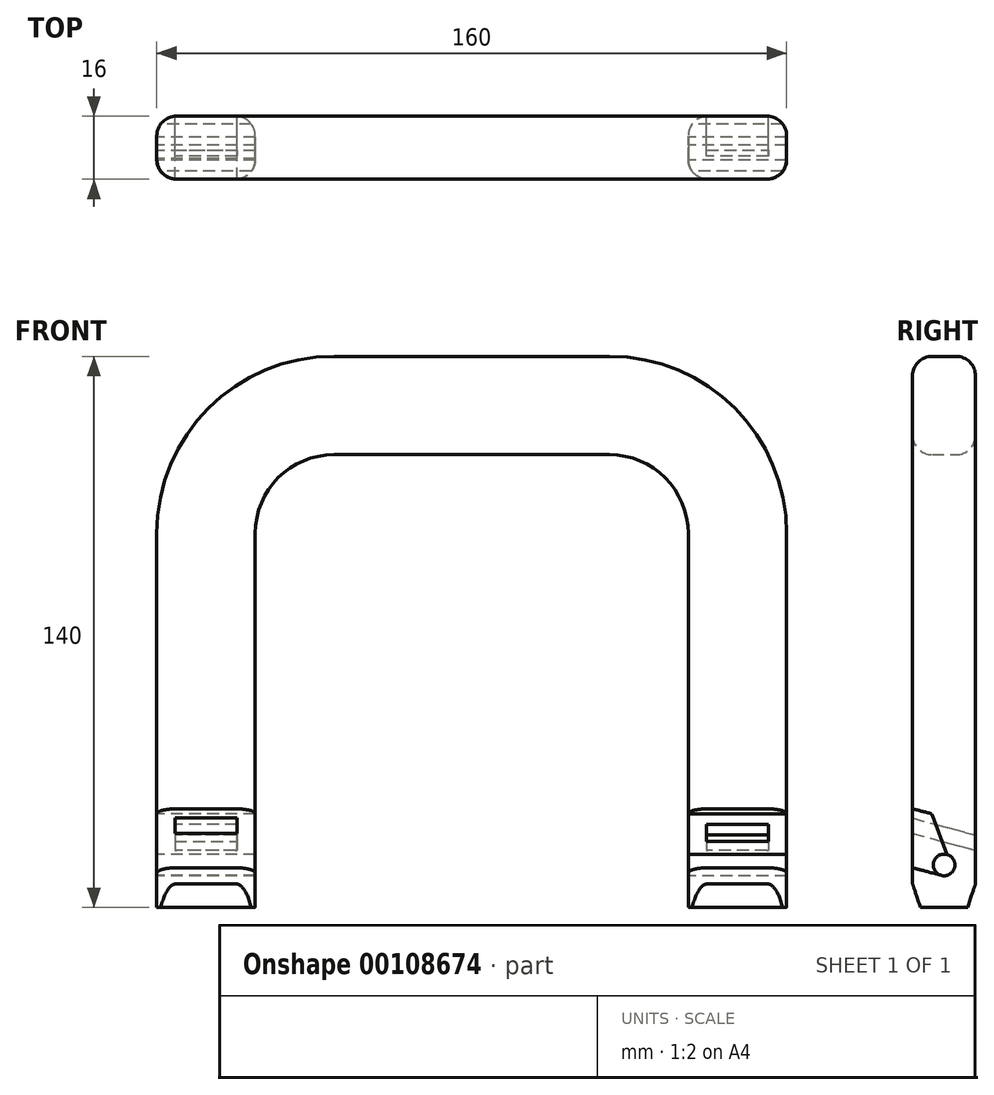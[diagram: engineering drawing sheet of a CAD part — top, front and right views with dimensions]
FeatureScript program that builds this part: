
annotation { "Feature Type Name" : "Feature", "Feature Type Description" : "" }
export const myFeature = defineFeature(function(context is Context, id is Id, definition is map)
    precondition{}
    {
        {
            var Q0;
            Q0=qCreatedBy(makeId("Front.planeOp"),FACE);
            var sketch = newSketch(context, id + "F0", { "sketchPlane" : qUnion([Q0])});
            skLineSegment(sketch, "E0.bottom", {"start": v(-80, 0) * mm, "end": v(80, 0) * mm});
            skLineSegment(sketch, "E0.top", {"start": v(-35, 140) * mm, "end": v(35, 140) * mm});
            skLineSegment(sketch, "E0.left", {"start": v(-80, 0) * mm, "end": v(-80, 95) * mm});
            skLineSegment(sketch, "E0.right", {"start": v(80, 0) * mm, "end": v(80, 95) * mm});
            skLineSegment(sketch, "E1.bottom", {"start": v(-55, 0) * mm, "end": v(55, 0) * mm});
            skLineSegment(sketch, "E1.top", {"start": v(-35, 115) * mm, "end": v(35, 115) * mm});
            skLineSegment(sketch, "E1.left", {"start": v(-55, 0) * mm, "end": v(-55, 95) * mm});
            skLineSegment(sketch, "E1.right", {"start": v(55, 0) * mm, "end": v(55, 95) * mm});
            skPoint(sketch, "E2.visualSharp", {"position": v(-80, 140) * mm});
            skArc(sketch, "E2.filletArc", {"start": v(-35, 140) * mm, "mid": v(-66.82, 126.82) * mm, "end": v(-80, 95) * mm});
            skPoint(sketch, "E3.visualSharp", {"position": v(80, 140) * mm});
            skArc(sketch, "E3.filletArc", {"start": v(80, 95) * mm, "mid": v(66.82, 126.82) * mm, "end": v(35, 140) * mm});
            skPoint(sketch, "E4.visualSharp", {"position": v(-55, 115) * mm});
            skArc(sketch, "E4.filletArc", {"start": v(-35, 115) * mm, "mid": v(-49.14, 109.14) * mm, "end": v(-55, 95) * mm});
            skPoint(sketch, "E5.visualSharp", {"position": v(55, 115) * mm});
            skArc(sketch, "E5.filletArc", {"start": v(55, 95) * mm, "mid": v(49.14, 109.14) * mm, "end": v(35, 115) * mm});
            skSolve(sketch);
        }
        {
            var Q0;
            Q0=makeQuery(id+"F0.imprint","IMPRINT",FACE,{"disambiguationData":[TD([[makeQuery(id+"F0.imprint","IMPRINT",EDGE,{"derivedFrom":sQuery(id+"F0.wireOp",EDGE,"E0.top")}),-1.0]])]});
            extrude(context, id + "F1", {"entities" : qUnion([Q0]), "depth" : 16 * mm});
        }
        {
            var Q0;
            Q0=makeQuery(id+"F1.opExtrude","SWEPT_FACE",FACE,{"disambiguationData":[OSD([sQuery(id+"F0.wireOp",EDGE,"E0.left")])]});
            var sketch = newSketch(context, id + "F2", { "sketchPlane" : qUnion([Q0])});
            skCircle(sketch, "E6", {"center": v(8, 10.75) * mm, "radius": 2.75 * mm});
            skLineSegment(sketch, "E7", {"start": v(8, 0) * mm, "end": v(8, 10.75) * mm, "construction": true});
            skLineSegment(sketch, "E8", {"start": v(8.71, 8.1) * mm, "end": v(16, 10.05) * mm});
            skLineSegment(sketch, "E9", {"start": v(16, 6) * mm, "end": v(14, 0) * mm});
            skLineSegment(sketch, "E10", {"start": v(2, 0) * mm, "end": v(0, 6) * mm});
            skLineSegment(sketch, "E11", {"start": v(11.17, 23.75) * mm, "end": v(16, 25.05) * mm});
            skLineSegment(sketch, "E12", {"start": v(8.71, 8.1) * mm, "end": v(8, 10.75) * mm, "construction": true});
            skLineSegment(sketch, "E13", {"start": v(8, 10.75) * mm, "end": v(7.29, 13.4) * mm, "construction": true});
            skLineSegment(sketch, "E14", {"start": v(7.29, 13.4) * mm, "end": v(11.17, 23.75) * mm});
            skLineSegment(sketch, "E15", {"start": v(11.17, 23.75) * mm, "end": v(0, 20.76) * mm});
            skSolve(sketch);
        }
        {
            var Q0;
            Q0 = qSketchRegion(id + "F2", true);
            var Q1;
            {var subQ0=sQuery(id+"F2.wireOp",EDGE,"E10");Q1=makeQuery(id+"F2.imprint","IMPRINT",FACE,{"disambiguationData":[TD([[makeQuery(id+"F2.imprint","IMPRINT",EDGE,{"derivedFrom":subQ0}),1.0]])]});}
            var Q2;
            {var subQ0=sQuery(id+"F2.wireOp",EDGE,"E9");Q2=makeQuery(id+"F2.imprint","IMPRINT",FACE,{"disambiguationData":[TD([[makeQuery(id+"F2.imprint","IMPRINT",EDGE,{"derivedFrom":subQ0}),1.0]])]});}
            var Q3;
            {var subQ0=sQuery(id+"F2.wireOp",EDGE,"E8");Q3=makeQuery(id+"F2.imprint","IMPRINT",FACE,{"disambiguationData":[TD([[makeQuery(id+"F2.imprint","IMPRINT",EDGE,{"derivedFrom":subQ0}),1.0]])]});}
            extrude(context, id + "F3", {"entities" : qUnion([Q0, Q1, Q2, Q3]), "operationType" : NewBodyOperationType.REMOVE, "endBound" : BoundingType.THROUGH_ALL, "oppositeDirection" : true, "depth" : 25 * mm});
        }
        {
            var Q0;
            {var subQ2=sQuery(id+"F2.wireOp",EDGE,"E8");Q0=makeQuery(id+"F2.imprint","IMPRINT",FACE,{"disambiguationData":[TD([[makeQuery(id+"F2.imprint","IMPRINT",EDGE,{"derivedFrom":subQ2}),1.0]])]});}
            extrude(context, id + "F4", {"entities" : qUnion([Q0]), "oppositeDirection" : true, "depth" : 25 * mm});
        }
        {
            var Q0;
            Q0=makeQuery(id+"F4.opExtrude","SWEPT_FACE",FACE,{"disambiguationData":[OSD([sQuery(id+"F0.wireOp",EDGE,"E0.left")])]});
            var sketch = newSketch(context, id + "F5", { "sketchPlane" : qUnion([Q0])});
            skLineSegment(sketch, "E16.bottom", {"start": v(-59.62, 22.65) * mm, "end": v(-75.38, 22.65) * mm});
            skLineSegment(sketch, "E16.top", {"start": v(-59.62, 18.76) * mm, "end": v(-75.38, 18.76) * mm});
            skLineSegment(sketch, "E16.left", {"start": v(-59.62, 22.65) * mm, "end": v(-59.62, 18.76) * mm});
            skLineSegment(sketch, "E16.right", {"start": v(-75.38, 22.65) * mm, "end": v(-75.38, 18.76) * mm});
            skPoint(sketch, "E16.middle", {"position": v(-67.5, 20.7) * mm});
            skLineSegment(sketch, "E17", {"start": v(-67.5, 10.05) * mm, "end": v(-67.5, 20.7) * mm, "construction": true});
            skSolve(sketch);
        }
        {
            var Q0;
            Q0=makeQuery(id+"F5.imprint","IMPRINT",FACE,{"disambiguationData":[TD([[makeQuery(id+"F5.imprint","IMPRINT",EDGE,{"derivedFrom":sQuery(id+"F5.wireOp",EDGE,"E16.bottom")}),1.0]])]});
            var Q1;
            Q1=sQuery(id+"F2.wireOp",EDGE,"E11");
            var Q2;
            Q2=sQuery(id+"F2.wireOp",EDGE,"E15");
            sweep(context, id + "F6", {"profiles" : qUnion([Q0]), "path" : qUnion([Q1, Q2])});
        }
        {
            var Q0;
            Q0=makeQuery(id+"F6.opSweep","SWEPT_BODY",BODY,{"disambiguationData":[OSD([sQuery(id+"F2.wireOp",EDGE,"E15"),sQuery(id+"F5.wireOp",EDGE,"E16.bottom"),sQuery(id+"F5.wireOp",EDGE,"E16.top"),sQuery(id+"F5.wireOp",EDGE,"E16.left"),sQuery(id+"F5.wireOp",EDGE,"E16.right")])]});
            var Q1;
            Q1=makeQuery(id+"F1.opExtrude","CAP_EDGE",EDGE,{"disambiguationData":[OSD([sQuery(id+"F0.wireOp",EDGE,"E0.top")])],"isStart":false});
            transform(context, id + "F7", {"entities" : qUnion([Q0]), "transformType" : TransformType.COPY});
        }
        {
            var Q0;
            Q0=makeQuery(id+"F7.opPattern","COPY",BODY,{"derivedFrom":makeQuery(id+"F6.opSweep","SWEPT_BODY",BODY,{"disambiguationData":[OSD([sQuery(id+"F2.wireOp",EDGE,"E15"),sQuery(id+"F5.wireOp",EDGE,"E16.bottom"),sQuery(id+"F5.wireOp",EDGE,"E16.top"),sQuery(id+"F5.wireOp",EDGE,"E16.left"),sQuery(id+"F5.wireOp",EDGE,"E16.right")])]}),"instanceName":"1"});
            transform(context, id + "F8", {"entities" : qUnion([Q0]), "transformType" : TransformType.COPY});
        }
        {
            var Q0;
            Q0=makeQuery(id+"F8.opPattern","COPY",BODY,{"derivedFrom":makeQuery(id+"F7.opPattern","COPY",BODY,{"derivedFrom":makeQuery(id+"F6.opSweep","SWEPT_BODY",BODY,{"disambiguationData":[OSD([sQuery(id+"F2.wireOp",EDGE,"E15"),sQuery(id+"F5.wireOp",EDGE,"E16.bottom"),sQuery(id+"F5.wireOp",EDGE,"E16.top"),sQuery(id+"F5.wireOp",EDGE,"E16.left"),sQuery(id+"F5.wireOp",EDGE,"E16.right")])]}),"instanceName":"1"}),"instanceName":"1"});
            var Q1;
            Q1=makeQuery(id+"F1.opExtrude","CAP_EDGE",EDGE,{"disambiguationData":[OSD([sQuery(id+"F0.wireOp",EDGE,"E1.top")])],"isStart":false});
            transform(context, id + "F9", {"entities" : qUnion([Q0]), "transformType" : TransformType.TRANSLATION_DISTANCE, "transformDirection" : qUnion([Q1]), "distance" : 135 * mm, "makeCopy" : false});
        }
        {
            var Q0;
            Q0=makeQuery(id+"F8.opPattern","COPY",BODY,{"derivedFrom":makeQuery(id+"F7.opPattern","COPY",BODY,{"derivedFrom":makeQuery(id+"F6.opSweep","SWEPT_BODY",BODY,{"disambiguationData":[OSD([sQuery(id+"F2.wireOp",EDGE,"E15"),sQuery(id+"F5.wireOp",EDGE,"E16.bottom"),sQuery(id+"F5.wireOp",EDGE,"E16.top"),sQuery(id+"F5.wireOp",EDGE,"E16.left"),sQuery(id+"F5.wireOp",EDGE,"E16.right")])]}),"instanceName":"1"}),"instanceName":"1"});
            var Q1;
            Q1=makeQuery(id+"F1.opExtrude","SWEPT_BODY",BODY,{"disambiguationData":[OSD([sQuery(id+"F0.wireOp",EDGE,"E0.bottom"),sQuery(id+"F0.wireOp",EDGE,"E0.top"),sQuery(id+"F0.wireOp",EDGE,"E0.left"),sQuery(id+"F0.wireOp",EDGE,"E0.right"),sQuery(id+"F0.wireOp",EDGE,"E1.top"),sQuery(id+"F0.wireOp",EDGE,"E1.left"),sQuery(id+"F0.wireOp",EDGE,"E1.right")])]});
            booleanBodies(context, id + "F10", {"operationType" : BooleanOperationType.SUBTRACTION, "tools" : qUnion([Q0]), "targets" : qUnion([Q1])});
        }
        {
            var Q0;
            Q0=makeQuery(id+"F7.opPattern","COPY",BODY,{"derivedFrom":makeQuery(id+"F6.opSweep","SWEPT_BODY",BODY,{"disambiguationData":[OSD([sQuery(id+"F2.wireOp",EDGE,"E15"),sQuery(id+"F5.wireOp",EDGE,"E16.bottom"),sQuery(id+"F5.wireOp",EDGE,"E16.top"),sQuery(id+"F5.wireOp",EDGE,"E16.left"),sQuery(id+"F5.wireOp",EDGE,"E16.right")])]}),"instanceName":"1"});
            var Q1;
            Q1=makeQuery(id+"F1.opExtrude","SWEPT_BODY",BODY,{"disambiguationData":[OSD([sQuery(id+"F0.wireOp",EDGE,"E0.bottom"),sQuery(id+"F0.wireOp",EDGE,"E0.top"),sQuery(id+"F0.wireOp",EDGE,"E0.left"),sQuery(id+"F0.wireOp",EDGE,"E0.right"),sQuery(id+"F0.wireOp",EDGE,"E1.top"),sQuery(id+"F0.wireOp",EDGE,"E1.left"),sQuery(id+"F0.wireOp",EDGE,"E1.right")])]});
            booleanBodies(context, id + "F11", {"operationType" : BooleanOperationType.SUBTRACTION, "tools" : qUnion([Q0]), "targets" : qUnion([Q1])});
        }
        {
            var Q0;
            Q0=makeQuery(id+"F1.opExtrude","CAP_EDGE",EDGE,{"disambiguationData":[OSD([sQuery(id+"F0.wireOp",EDGE,"E1.top")])],"isStart":false});
            var Q1;
            Q1=makeQuery(id+"F1.opExtrude","CAP_EDGE",EDGE,{"disambiguationData":[OSD([sQuery(id+"F0.wireOp",EDGE,"E1.top")])],"isStart":true});
            var Q2;
            Q2=makeQuery(id+"F1.opExtrude","CAP_EDGE",EDGE,{"disambiguationData":[OSD([sQuery(id+"F0.wireOp",EDGE,"E0.top")])],"isStart":false});
            var Q3;
            Q3=makeQuery(id+"F1.opExtrude","CAP_EDGE",EDGE,{"disambiguationData":[OSD([sQuery(id+"F0.wireOp",EDGE,"E0.top")])],"isStart":true});
            var Q4;
            {var subQ0=sQuery(id+"F0.wireOp",EDGE,"E0.left");Q4=makeQuery(id+"F3.boolean.opBoolean","SPLIT",EDGE,{"disambiguationData":[TD([makeQuery(id+"F3.opExtrude","SWEPT_FACE",FACE,{"disambiguationData":[OSD([sQuery(id+"F2.wireOp",EDGE,"E8")])]})])],"derivedFrom":makeQuery(id+"F1.opExtrude","CAP_EDGE",EDGE,{"disambiguationData":[OSD([subQ0])],"isStart":false})});}
            var Q5;
            {var subQ0=sQuery(id+"F0.wireOp",EDGE,"E1.left");Q5=makeQuery(id+"F3.boolean.opBoolean","SPLIT",EDGE,{"disambiguationData":[TD([makeQuery(id+"F3.opExtrude","SWEPT_FACE",FACE,{"disambiguationData":[OSD([sQuery(id+"F2.wireOp",EDGE,"E8")])]})])],"derivedFrom":makeQuery(id+"F1.opExtrude","CAP_EDGE",EDGE,{"disambiguationData":[OSD([subQ0])],"isStart":false})});}
            var Q6;
            {var subQ0=sQuery(id+"F0.wireOp",EDGE,"E1.right");Q6=makeQuery(id+"F3.boolean.opBoolean","SPLIT",EDGE,{"disambiguationData":[TD([makeQuery(id+"F3.opExtrude","SWEPT_FACE",FACE,{"disambiguationData":[OSD([sQuery(id+"F2.wireOp",EDGE,"E8")])]})])],"derivedFrom":makeQuery(id+"F1.opExtrude","CAP_EDGE",EDGE,{"disambiguationData":[OSD([subQ0])],"isStart":false})});}
            var Q7;
            {var subQ0=sQuery(id+"F0.wireOp",EDGE,"E0.right");Q7=makeQuery(id+"F3.boolean.opBoolean","SPLIT",EDGE,{"disambiguationData":[TD([makeQuery(id+"F3.opExtrude","SWEPT_FACE",FACE,{"disambiguationData":[OSD([sQuery(id+"F2.wireOp",EDGE,"E8")])]})])],"derivedFrom":makeQuery(id+"F1.opExtrude","CAP_EDGE",EDGE,{"disambiguationData":[OSD([subQ0])],"isStart":false})});}
            var Q8;
            Q8=makeQuery(id+"F3.boolean.opBoolean","COPY",EDGE,{"disambiguationData":[OD(1.0)],"derivedFrom":makeQuery(id+"F3.opExtrude","SWEPT_EDGE",EDGE,{"disambiguationData":[OSD([sQuery(id+"F0.wireOp",EDGE,"E0.bottom"),sQuery(id+"F0.wireOp",EDGE,"E0.left"),sQuery(id+"F2.wireOp",EDGE,"E9")])]})});
            var Q9;
            Q9=makeQuery(id+"F3.boolean.opBoolean","COPY",EDGE,{"disambiguationData":[OD(1.0)],"derivedFrom":makeQuery(id+"F3.opExtrude","SWEPT_EDGE",EDGE,{"disambiguationData":[OSD([sQuery(id+"F0.wireOp",EDGE,"E0.bottom"),sQuery(id+"F0.wireOp",EDGE,"E0.left"),sQuery(id+"F2.wireOp",EDGE,"E10")])]})});
            var Q10;
            Q10=makeQuery(id+"F3.boolean.opBoolean","COPY",EDGE,{"disambiguationData":[OD(0.0)],"derivedFrom":makeQuery(id+"F3.opExtrude","SWEPT_EDGE",EDGE,{"disambiguationData":[OSD([sQuery(id+"F0.wireOp",EDGE,"E0.bottom"),sQuery(id+"F0.wireOp",EDGE,"E0.left"),sQuery(id+"F2.wireOp",EDGE,"E9")])]})});
            var Q11;
            Q11=makeQuery(id+"F3.boolean.opBoolean","COPY",EDGE,{"disambiguationData":[OD(0.0)],"derivedFrom":makeQuery(id+"F3.opExtrude","SWEPT_EDGE",EDGE,{"disambiguationData":[OSD([sQuery(id+"F0.wireOp",EDGE,"E0.bottom"),sQuery(id+"F0.wireOp",EDGE,"E0.left"),sQuery(id+"F2.wireOp",EDGE,"E10")])]})});
            var Q12;
            Q12=makeQuery(id+"F4.opExtrude","CAP_EDGE",EDGE,{"disambiguationData":[OSD([sQuery(id+"F0.wireOp",EDGE,"E0.left")])],"isStart":true});
            var Q13;
            Q13=makeQuery(id+"F4.opExtrude","CAP_EDGE",EDGE,{"disambiguationData":[OSD([sQuery(id+"F0.wireOp",EDGE,"E0.left")])],"isStart":false});
            fillet(context, id + "F12", {"entities" : qUnion([Q0, Q1, Q2, Q3, Q4, Q5, Q6, Q7, Q8, Q9, Q10, Q11, Q12, Q13]), "radius" : 5 * mm, "tangentPropagation" : true, "allowEdgeOverflow" : false});
        }
    });
